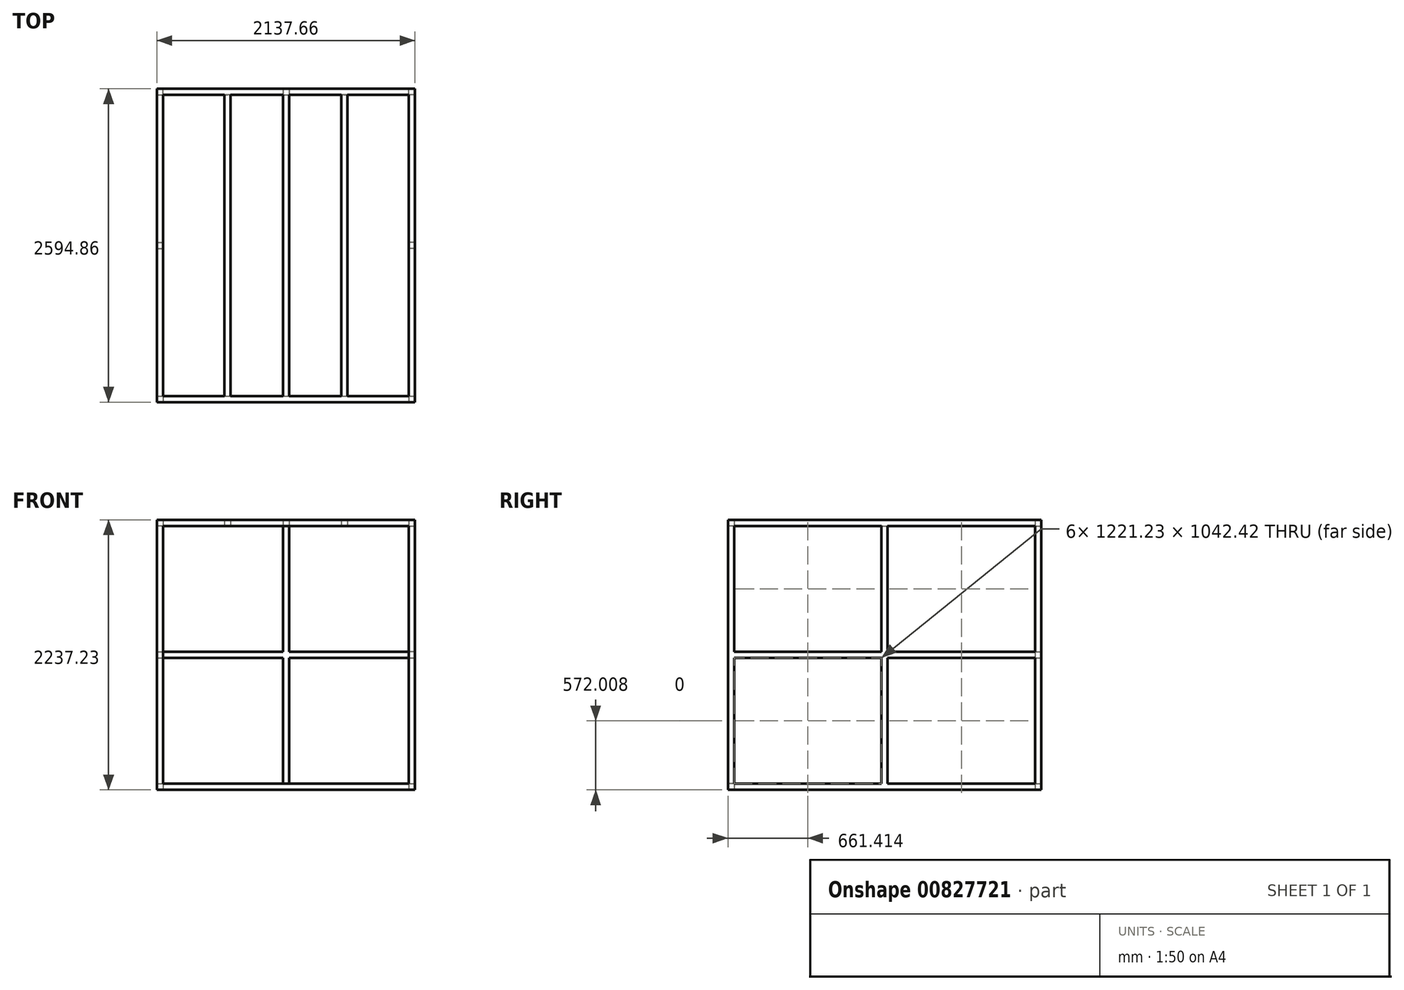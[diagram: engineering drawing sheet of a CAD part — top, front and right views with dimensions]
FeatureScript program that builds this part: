
annotation { "Feature Type Name" : "Feature", "Feature Type Description" : "" }
export const myFeature = defineFeature(function(context is Context, id is Id, definition is map)
    precondition{}
    {
        {
            var Q0;
            Q0=qCreatedBy(makeId("Top.planeOp"),FACE);
            var sketch = newSketch(context, id + "F0", { "sketchPlane" : qUnion([Q0])});
            skLineSegment(sketch, "E0.bottom", {"start": v(-1018.03, 1246.63) * mm, "end": v(1018.03, 1246.63) * mm});
            skLineSegment(sketch, "E0.top", {"start": v(-1018.03, -1246.63) * mm, "end": v(1018.03, -1246.63) * mm});
            skLineSegment(sketch, "E0.left", {"start": v(-1018.03, 1246.63) * mm, "end": v(-1018.03, -1246.63) * mm});
            skLineSegment(sketch, "E0.right", {"start": v(1018.03, 1246.63) * mm, "end": v(1018.03, -1246.63) * mm});
            skPoint(sketch, "E0.middle", {"position": v(0, 0) * mm});
            skLineSegment(sketch, "E1.bottom", {"start": v(-1068.83, 1297.43) * mm, "end": v(1068.83, 1297.43) * mm});
            skLineSegment(sketch, "E1.top", {"start": v(-1068.83, -1297.43) * mm, "end": v(1068.83, -1297.43) * mm});
            skLineSegment(sketch, "E1.left", {"start": v(-1068.83, 1297.43) * mm, "end": v(-1068.83, -1297.43) * mm});
            skLineSegment(sketch, "E1.right", {"start": v(1068.83, 1297.43) * mm, "end": v(1068.83, -1297.43) * mm});
            skLineSegment(sketch, "E2.bottom", {"start": v(-510.03, 1246.63) * mm, "end": v(-459.23, 1246.63) * mm});
            skLineSegment(sketch, "E2.top", {"start": v(-510.03, -1246.63) * mm, "end": v(-459.23, -1246.63) * mm});
            skLineSegment(sketch, "E2.left", {"start": v(-510.03, 1246.63) * mm, "end": v(-510.03, -1246.63) * mm});
            skLineSegment(sketch, "E2.right", {"start": v(-459.23, 1246.63) * mm, "end": v(-459.23, -1246.63) * mm});
            skLineSegment(sketch, "E3.bottom", {"start": v(459.23, -1246.63) * mm, "end": v(510.03, -1246.63) * mm});
            skLineSegment(sketch, "E3.top", {"start": v(459.23, 1246.63) * mm, "end": v(510.03, 1246.63) * mm});
            skLineSegment(sketch, "E3.left", {"start": v(459.23, -1246.63) * mm, "end": v(459.23, 1246.63) * mm});
            skLineSegment(sketch, "E3.right", {"start": v(510.03, -1246.63) * mm, "end": v(510.03, 1246.63) * mm});
            skLineSegment(sketch, "E4.bottom", {"start": v(-25.4, 1246.63) * mm, "end": v(25.4, 1246.63) * mm});
            skLineSegment(sketch, "E4.top", {"start": v(-25.4, -1246.63) * mm, "end": v(25.4, -1246.63) * mm});
            skLineSegment(sketch, "E4.left", {"start": v(-25.4, 1246.63) * mm, "end": v(-25.4, -1246.63) * mm});
            skLineSegment(sketch, "E4.right", {"start": v(25.4, 1246.63) * mm, "end": v(25.4, -1246.63) * mm});
            skSolve(sketch);
        }
        {
            var Q0;
            Q0=makeQuery(id+"F0.imprint","IMPRINT",FACE,{"disambiguationData":[TD([[makeQuery(id+"F0.imprint","IMPRINT",EDGE,{"derivedFrom":sQuery(id+"F0.wireOp",EDGE,"E0.bottom")}),1.0]])]});
            var Q1;
            Q1=makeQuery(id+"F0.imprint","IMPRINT",FACE,{"disambiguationData":[TD([[makeQuery(id+"F0.imprint","IMPRINT",EDGE,{"derivedFrom":sQuery(id+"F0.wireOp",EDGE,"E2.bottom")}),-1.0]])]});
            var Q2;
            Q2=makeQuery(id+"F0.imprint","IMPRINT",FACE,{"disambiguationData":[TD([[makeQuery(id+"F0.imprint","IMPRINT",EDGE,{"derivedFrom":sQuery(id+"F0.wireOp",EDGE,"E4.bottom")}),-1.0]])]});
            var Q3;
            Q3=makeQuery(id+"F0.imprint","IMPRINT",FACE,{"disambiguationData":[TD([[makeQuery(id+"F0.imprint","IMPRINT",EDGE,{"derivedFrom":sQuery(id+"F0.wireOp",EDGE,"E3.bottom")}),1.0]])]});
            extrude(context, id + "F1", {"entities" : qUnion([Q0, Q1, Q2, Q3]), "depth" : 50.8 * mm, "offsetDistance" : 25.4 * mm});
        }
        {
            var Q0;
            Q0=makeQuery(id+"F1.opExtrude","CAP_FACE",FACE,{"disambiguationData":[OSD([sQuery(id+"F0.wireOp",EDGE,"E0.bottom"),sQuery(id+"F0.wireOp",EDGE,"E0.top"),sQuery(id+"F0.wireOp",EDGE,"E0.left"),sQuery(id+"F0.wireOp",EDGE,"E0.right"),sQuery(id+"F0.wireOp",EDGE,"E1.bottom"),sQuery(id+"F0.wireOp",EDGE,"E1.top"),sQuery(id+"F0.wireOp",EDGE,"E1.left"),sQuery(id+"F0.wireOp",EDGE,"E1.right")])],"isStart":false});
            var sketch = newSketch(context, id + "F2", { "sketchPlane" : qUnion([Q0])});
            skLineSegment(sketch, "E5.bottom", {"start": v(-1018.03, 1246.63) * mm, "end": v(-1068.83, 1246.63) * mm});
            skLineSegment(sketch, "E5.top", {"start": v(-1018.03, 1297.43) * mm, "end": v(-1068.83, 1297.43) * mm});
            skLineSegment(sketch, "E5.left", {"start": v(-1018.03, 1246.63) * mm, "end": v(-1018.03, 1297.43) * mm});
            skLineSegment(sketch, "E5.right", {"start": v(-1068.83, 1246.63) * mm, "end": v(-1068.83, 1297.43) * mm});
            skLineSegment(sketch, "E6.bottom", {"start": v(1018.03, 1246.63) * mm, "end": v(1068.83, 1246.63) * mm});
            skLineSegment(sketch, "E6.top", {"start": v(1018.03, 1297.43) * mm, "end": v(1068.83, 1297.43) * mm});
            skLineSegment(sketch, "E6.left", {"start": v(1018.03, 1246.63) * mm, "end": v(1018.03, 1297.43) * mm});
            skLineSegment(sketch, "E6.right", {"start": v(1068.83, 1246.63) * mm, "end": v(1068.83, 1297.43) * mm});
            skLineSegment(sketch, "E7.bottom", {"start": v(1018.03, -1246.63) * mm, "end": v(1068.83, -1246.63) * mm});
            skLineSegment(sketch, "E7.top", {"start": v(1018.03, -1297.43) * mm, "end": v(1068.83, -1297.43) * mm});
            skLineSegment(sketch, "E7.left", {"start": v(1018.03, -1246.63) * mm, "end": v(1018.03, -1297.43) * mm});
            skLineSegment(sketch, "E7.right", {"start": v(1068.83, -1246.63) * mm, "end": v(1068.83, -1297.43) * mm});
            skLineSegment(sketch, "E8.bottom", {"start": v(-1018.03, -1246.63) * mm, "end": v(-1068.83, -1246.63) * mm});
            skLineSegment(sketch, "E8.top", {"start": v(-1018.03, -1297.43) * mm, "end": v(-1068.83, -1297.43) * mm});
            skLineSegment(sketch, "E8.left", {"start": v(-1018.03, -1246.63) * mm, "end": v(-1018.03, -1297.43) * mm});
            skLineSegment(sketch, "E8.right", {"start": v(-1068.83, -1246.63) * mm, "end": v(-1068.83, -1297.43) * mm});
            skLineSegment(sketch, "E9.bottom", {"start": v(-1068.83, 25.4) * mm, "end": v(-1018.03, 25.4) * mm});
            skLineSegment(sketch, "E9.top", {"start": v(-1068.83, -25.4) * mm, "end": v(-1018.03, -25.4) * mm});
            skLineSegment(sketch, "E9.left", {"start": v(-1068.83, 25.4) * mm, "end": v(-1068.83, -25.4) * mm});
            skLineSegment(sketch, "E9.right", {"start": v(-1018.03, 25.4) * mm, "end": v(-1018.03, -25.4) * mm});
            skLineSegment(sketch, "E10.bottom", {"start": v(1018.03, -25.4) * mm, "end": v(1068.83, -25.4) * mm});
            skLineSegment(sketch, "E10.top", {"start": v(1018.03, 25.4) * mm, "end": v(1068.83, 25.4) * mm});
            skLineSegment(sketch, "E10.left", {"start": v(1018.03, -25.4) * mm, "end": v(1018.03, 25.4) * mm});
            skLineSegment(sketch, "E10.right", {"start": v(1068.83, -25.4) * mm, "end": v(1068.83, 25.4) * mm});
            skLineSegment(sketch, "E11.bottom", {"start": v(-25.4, 1297.43) * mm, "end": v(25.4, 1297.43) * mm});
            skLineSegment(sketch, "E11.top", {"start": v(-25.4, 1246.63) * mm, "end": v(25.4, 1246.63) * mm});
            skLineSegment(sketch, "E11.left", {"start": v(-25.4, 1297.43) * mm, "end": v(-25.4, 1246.63) * mm});
            skLineSegment(sketch, "E11.right", {"start": v(25.4, 1297.43) * mm, "end": v(25.4, 1246.63) * mm});
            skSolve(sketch);
        }
        {
            var Q0;
            Q0=makeQuery(id+"F2.imprint","IMPRINT",FACE,{"disambiguationData":[TD([[makeQuery(id+"F2.imprint","IMPRINT",EDGE,{"derivedFrom":sQuery(id+"F2.wireOp",EDGE,"E5.bottom")}),-1.0]])]});
            var Q1;
            Q1=makeQuery(id+"F2.imprint","IMPRINT",FACE,{"disambiguationData":[TD([[makeQuery(id+"F2.imprint","IMPRINT",EDGE,{"derivedFrom":sQuery(id+"F2.wireOp",EDGE,"E6.bottom")}),1.0]])]});
            var Q2;
            Q2=makeQuery(id+"F2.imprint","IMPRINT",FACE,{"disambiguationData":[TD([[makeQuery(id+"F2.imprint","IMPRINT",EDGE,{"derivedFrom":sQuery(id+"F2.wireOp",EDGE,"E7.bottom")}),-1.0]])]});
            var Q3;
            Q3=makeQuery(id+"F2.imprint","IMPRINT",FACE,{"disambiguationData":[TD([[makeQuery(id+"F2.imprint","IMPRINT",EDGE,{"derivedFrom":sQuery(id+"F2.wireOp",EDGE,"E8.bottom")}),1.0]])]});
            var Q4;
            Q4=makeQuery(id+"F2.imprint","IMPRINT",FACE,{"disambiguationData":[TD([[makeQuery(id+"F2.imprint","IMPRINT",EDGE,{"derivedFrom":sQuery(id+"F2.wireOp",EDGE,"E9.bottom")}),-1.0]])]});
            var Q5;
            Q5=makeQuery(id+"F2.imprint","IMPRINT",FACE,{"disambiguationData":[TD([[makeQuery(id+"F2.imprint","IMPRINT",EDGE,{"derivedFrom":sQuery(id+"F2.wireOp",EDGE,"E10.bottom")}),1.0]])]});
            var Q6;
            Q6=makeQuery(id+"F2.imprint","IMPRINT",FACE,{"disambiguationData":[TD([[makeQuery(id+"F2.imprint","IMPRINT",EDGE,{"derivedFrom":sQuery(id+"F2.wireOp",EDGE,"E11.bottom")}),-1.0]])]});
            extrude(context, id + "F3", {"entities" : qUnion([Q0, Q1, Q2, Q3, Q4, Q5, Q6]), "operationType" : NewBodyOperationType.ADD, "depth" : 2135.63 * mm, "offsetDistance" : 25.4 * mm});
        }
        {
            var Q0;
            Q0=makeQuery(id+"F3.opExtrude","CAP_FACE",FACE,{"disambiguationData":[OSD([sQuery(id+"F2.wireOp",EDGE,"E5.bottom"),sQuery(id+"F2.wireOp",EDGE,"E5.top"),sQuery(id+"F2.wireOp",EDGE,"E5.left"),sQuery(id+"F2.wireOp",EDGE,"E5.right")])],"isStart":false});
            var sketch = newSketch(context, id + "F4", { "sketchPlane" : qUnion([Q0])});
            skLineSegment(sketch, "E12.0", {"start": v(-1068.83, 1246.63) * mm, "end": v(-1068.83, 25.4) * mm});
            skLineSegment(sketch, "E13.0", {"start": v(-1018.03, 1246.63) * mm, "end": v(-1018.03, 25.4) * mm});
            skLineSegment(sketch, "E14.0", {"start": v(-1018.03, 1246.63) * mm, "end": v(-510.03, 1246.63) * mm});
            skLineSegment(sketch, "E15.0", {"start": v(-1018.03, 1297.43) * mm, "end": v(-25.4, 1297.43) * mm});
            skLineSegment(sketch, "E16.0", {"start": v(-510.03, 1246.63) * mm, "end": v(-510.03, -1246.63) * mm});
            skLineSegment(sketch, "E17.0", {"start": v(-459.23, 1246.63) * mm, "end": v(-25.4, 1246.63) * mm});
            skLineSegment(sketch, "E18.0", {"start": v(-25.4, 1246.63) * mm, "end": v(-25.4, -1246.63) * mm});
            skLineSegment(sketch, "E19.0", {"start": v(25.4, 1246.63) * mm, "end": v(25.4, -1246.63) * mm});
            skLineSegment(sketch, "E20.0.0", {"start": v(1018.03, 1297.43) * mm, "end": v(25.4, 1297.43) * mm});
            skLineSegment(sketch, "E20.0.2", {"start": v(25.4, 1246.63) * mm, "end": v(459.23, 1246.63) * mm});
            skLineSegment(sketch, "E20.0.3", {"start": v(459.23, 1246.63) * mm, "end": v(459.23, -1246.63) * mm});
            skLineSegment(sketch, "E20.0.4", {"start": v(459.23, -1246.63) * mm, "end": v(25.4, -1246.63) * mm});
            skLineSegment(sketch, "E20.0.5", {"start": v(25.4, -1246.63) * mm, "end": v(25.4, 1246.63) * mm});
            skLineSegment(sketch, "E20.0.8", {"start": v(-25.4, -1246.63) * mm, "end": v(-459.23, -1246.63) * mm});
            skLineSegment(sketch, "E20.0.9", {"start": v(-459.23, -1246.63) * mm, "end": v(-459.23, 1246.63) * mm});
            skLineSegment(sketch, "E20.0.12", {"start": v(-25.4, 1297.43) * mm, "end": v(-1018.03, 1297.43) * mm});
            skLineSegment(sketch, "E20.0.16", {"start": v(-510.03, -1246.63) * mm, "end": v(-1018.03, -1246.63) * mm});
            skLineSegment(sketch, "E20.0.18", {"start": v(-1018.03, -1297.43) * mm, "end": v(1018.03, -1297.43) * mm});
            skLineSegment(sketch, "E20.0.20", {"start": v(1018.03, -1246.63) * mm, "end": v(510.03, -1246.63) * mm});
            skLineSegment(sketch, "E20.0.21", {"start": v(510.03, -1246.63) * mm, "end": v(510.03, 1246.63) * mm});
            skLineSegment(sketch, "E20.0.22", {"start": v(510.03, 1246.63) * mm, "end": v(1018.03, 1246.63) * mm});
            skPoint(sketch, "E21.0", {"position": v(0, 1297.43) * mm});
            skLineSegment(sketch, "E22.0", {"start": v(1068.83, -25.4) * mm, "end": v(1068.83, -1246.63) * mm});
            skLineSegment(sketch, "E23.0.1", {"start": v(1018.03, -25.4) * mm, "end": v(1018.03, -1246.63) * mm});
            skLineSegment(sketch, "E23.0.3", {"start": v(1068.83, -1246.63) * mm, "end": v(1068.83, -25.4) * mm});
            skLineSegment(sketch, "E24.0", {"start": v(1018.03, 25.4) * mm, "end": v(1018.03, -25.4) * mm});
            skLineSegment(sketch, "E25.0", {"start": v(1068.83, 25.4) * mm, "end": v(1068.83, -25.4) * mm});
            skLineSegment(sketch, "E26.0", {"start": v(1018.03, 1246.63) * mm, "end": v(1018.03, 25.4) * mm});
            skLineSegment(sketch, "E27.0", {"start": v(1068.83, 1246.63) * mm, "end": v(1068.83, 25.4) * mm});
            skLineSegment(sketch, "E28.0", {"start": v(1018.03, 1297.43) * mm, "end": v(1068.83, 1297.43) * mm});
            skLineSegment(sketch, "E29.0", {"start": v(1068.83, 1297.43) * mm, "end": v(1068.83, 1246.63) * mm});
            skLineSegment(sketch, "E30.0", {"start": v(-1068.83, -1246.63) * mm, "end": v(-1068.83, -1297.43) * mm});
            skLineSegment(sketch, "E31.0", {"start": v(-1068.83, -1297.43) * mm, "end": v(-1018.03, -1297.43) * mm});
            skLineSegment(sketch, "E32.0", {"start": v(-1018.03, -25.4) * mm, "end": v(-1018.03, -1246.63) * mm});
            skLineSegment(sketch, "E33.0", {"start": v(-1068.83, -25.4) * mm, "end": v(-1068.83, -1246.63) * mm});
            skLineSegment(sketch, "E34.0", {"start": v(-1068.83, 25.4) * mm, "end": v(-1068.83, -25.4) * mm});
            skLineSegment(sketch, "E35.0", {"start": v(-1018.03, 25.4) * mm, "end": v(-1018.03, -25.4) * mm});
            skLineSegment(sketch, "E36", {"start": v(25.4, 1297.43) * mm, "end": v(-25.4, 1297.43) * mm});
            skLineSegment(sketch, "E37", {"start": v(1018.03, -1297.43) * mm, "end": v(1068.83, -1297.43) * mm});
            skLineSegment(sketch, "E38", {"start": v(1068.83, -1297.43) * mm, "end": v(1068.83, -1246.63) * mm});
            skLineSegment(sketch, "E39", {"start": v(-1068.83, 1246.63) * mm, "end": v(-1068.83, 1297.43) * mm});
            skLineSegment(sketch, "E40", {"start": v(-1068.83, 1297.43) * mm, "end": v(-1018.03, 1297.43) * mm});
            skSolve(sketch);
        }
        {
            var Q0;
            Q0 = qSketchRegion(id + "F4", true);
            extrude(context, id + "F5", {"entities" : qUnion([Q0]), "operationType" : NewBodyOperationType.ADD, "depth" : 50.8 * mm, "offsetDistance" : 25.4 * mm});
        }
        {
            var Q0;
            Q0=makeQuery(id+"F3.opExtrude","SWEPT_FACE",FACE,{"disambiguationData":[OSD([sQuery(id+"F2.wireOp",EDGE,"E5.bottom")])]});
            var sketch = newSketch(context, id + "F6", { "sketchPlane" : qUnion([Q0])});
            skLineSegment(sketch, "E41.bottom", {"start": v(-1068.83, 1093.22) * mm, "end": v(-1018.03, 1093.22) * mm});
            skLineSegment(sketch, "E41.top", {"start": v(-1068.83, 1144.02) * mm, "end": v(-1018.03, 1144.02) * mm});
            skLineSegment(sketch, "E41.left", {"start": v(-1068.83, 1093.22) * mm, "end": v(-1068.83, 1144.02) * mm});
            skLineSegment(sketch, "E41.right", {"start": v(-1018.03, 1093.22) * mm, "end": v(-1018.03, 1144.02) * mm});
            skSolve(sketch);
        }
        {
            var Q0;
            Q0=makeQuery(id+"F6.imprint","IMPRINT",FACE,{"disambiguationData":[TD([[makeQuery(id+"F6.imprint","IMPRINT",EDGE,{"derivedFrom":sQuery(id+"F6.wireOp",EDGE,"E41.bottom")}),1.0]])]});
            var Q1;
            Q1=makeQuery(id+"F3.opExtrude","SWEPT_FACE",FACE,{"disambiguationData":[OSD([sQuery(id+"F2.wireOp",EDGE,"E8.bottom")])]});
            extrude(context, id + "F7", {"entities" : qUnion([Q0]), "operationType" : NewBodyOperationType.ADD, "endBound" : BoundingType.UP_TO_SURFACE, "depth" : 25.4 * mm, "endBoundEntityFace" : qUnion([Q1]), "offsetDistance" : 25.4 * mm});
        }
        {
            var Q0;
            Q0=makeQuery(id+"F3.opExtrude","SWEPT_FACE",FACE,{"disambiguationData":[OSD([sQuery(id+"F2.wireOp",EDGE,"E6.bottom")])]});
            var sketch = newSketch(context, id + "F8", { "sketchPlane" : qUnion([Q0])});
            skLineSegment(sketch, "E42.bottom", {"start": v(1068.83, 1093.22) * mm, "end": v(1018.03, 1093.22) * mm});
            skLineSegment(sketch, "E42.top", {"start": v(1068.83, 1144.02) * mm, "end": v(1018.03, 1144.02) * mm});
            skLineSegment(sketch, "E42.left", {"start": v(1068.83, 1093.22) * mm, "end": v(1068.83, 1144.02) * mm});
            skLineSegment(sketch, "E42.right", {"start": v(1018.03, 1093.22) * mm, "end": v(1018.03, 1144.02) * mm});
            skSolve(sketch);
        }
        {
            var Q0;
            Q0=makeQuery(id+"F8.imprint","IMPRINT",FACE,{"disambiguationData":[TD([[makeQuery(id+"F8.imprint","IMPRINT",EDGE,{"derivedFrom":sQuery(id+"F8.wireOp",EDGE,"E42.bottom")}),-1.0]])]});
            var Q1;
            Q1=makeQuery(id+"F3.opExtrude","SWEPT_FACE",FACE,{"disambiguationData":[OSD([sQuery(id+"F2.wireOp",EDGE,"E7.bottom")])]});
            extrude(context, id + "F9", {"entities" : qUnion([Q0]), "operationType" : NewBodyOperationType.ADD, "endBound" : BoundingType.UP_TO_SURFACE, "depth" : 25.4 * mm, "endBoundEntityFace" : qUnion([Q1]), "offsetDistance" : 25.4 * mm});
        }
        {
            var Q0;
            Q0=makeQuery(id+"F7.boolean.opBoolean","MERGE",FACE,{"derivedFrom":[makeQuery(id+"F3.opExtrude","SWEPT_FACE",FACE,{"disambiguationData":[OSD([sQuery(id+"F2.wireOp",EDGE,"E5.left")])]}),makeQuery(id+"F3.opExtrude","SWEPT_FACE",FACE,{"disambiguationData":[OSD([sQuery(id+"F2.wireOp",EDGE,"E8.left")])]}),makeQuery(id+"F5.boolean.opBoolean","MERGE",FACE,{"derivedFrom":[makeQuery(id+"F3.boolean.opBoolean","MERGE",FACE,{"derivedFrom":[makeQuery(id+"F1.opExtrude","SWEPT_FACE",FACE,{"disambiguationData":[OSD([sQuery(id+"F0.wireOp",EDGE,"E0.left")])]}),makeQuery(id+"F3.opExtrude","SWEPT_FACE",FACE,{"disambiguationData":[OSD([sQuery(id+"F2.wireOp",EDGE,"E9.right")])]})]}),makeQuery(id+"F5.opExtrude","SWEPT_FACE",FACE,{"disambiguationData":[OSD([sQuery(id+"F4.wireOp",EDGE,"E13.0"),sQuery(id+"F4.wireOp",EDGE,"E32.0"),sQuery(id+"F4.wireOp",EDGE,"E35.0")])]})]}),makeQuery(id+"F7.opExtrude","SWEPT_FACE",FACE,{"disambiguationData":[OSD([sQuery(id+"F6.wireOp",EDGE,"E41.right")])]})]});
            var sketch = newSketch(context, id + "F10", { "sketchPlane" : qUnion([Q0])});
            skLineSegment(sketch, "E43.bottom", {"start": v(1246.63, 1144.02) * mm, "end": v(1297.43, 1144.02) * mm});
            skLineSegment(sketch, "E43.top", {"start": v(1246.63, 1093.22) * mm, "end": v(1297.43, 1093.22) * mm});
            skLineSegment(sketch, "E43.left", {"start": v(1246.63, 1144.02) * mm, "end": v(1246.63, 1093.22) * mm});
            skLineSegment(sketch, "E43.right", {"start": v(1297.43, 1144.02) * mm, "end": v(1297.43, 1093.22) * mm});
            skSolve(sketch);
        }
        {
            var Q0;
            Q0=makeQuery(id+"F10.imprint","IMPRINT",FACE,{"disambiguationData":[TD([[makeQuery(id+"F10.imprint","IMPRINT",EDGE,{"derivedFrom":sQuery(id+"F10.wireOp",EDGE,"E43.bottom")}),-1.0]])]});
            var Q1;
            Q1=makeQuery(id+"F9.boolean.opBoolean","MERGE",FACE,{"derivedFrom":[makeQuery(id+"F3.opExtrude","SWEPT_FACE",FACE,{"disambiguationData":[OSD([sQuery(id+"F2.wireOp",EDGE,"E6.left")])]}),makeQuery(id+"F3.opExtrude","SWEPT_FACE",FACE,{"disambiguationData":[OSD([sQuery(id+"F2.wireOp",EDGE,"E7.left")])]}),makeQuery(id+"F5.boolean.opBoolean","MERGE",FACE,{"derivedFrom":[makeQuery(id+"F3.boolean.opBoolean","MERGE",FACE,{"derivedFrom":[makeQuery(id+"F1.opExtrude","SWEPT_FACE",FACE,{"disambiguationData":[OSD([sQuery(id+"F0.wireOp",EDGE,"E0.right")])]}),makeQuery(id+"F3.opExtrude","SWEPT_FACE",FACE,{"disambiguationData":[OSD([sQuery(id+"F2.wireOp",EDGE,"E10.left")])]})]}),makeQuery(id+"F5.opExtrude","SWEPT_FACE",FACE,{"disambiguationData":[OSD([sQuery(id+"F4.wireOp",EDGE,"E23.0.1"),sQuery(id+"F4.wireOp",EDGE,"E24.0"),sQuery(id+"F4.wireOp",EDGE,"E26.0")])]})]}),makeQuery(id+"F9.opExtrude","SWEPT_FACE",FACE,{"disambiguationData":[OSD([sQuery(id+"F8.wireOp",EDGE,"E42.right")])]})]});
            extrude(context, id + "F11", {"entities" : qUnion([Q0]), "operationType" : NewBodyOperationType.ADD, "endBound" : BoundingType.UP_TO_SURFACE, "depth" : 25.4 * mm, "endBoundEntityFace" : qUnion([Q1]), "offsetDistance" : 25.4 * mm});
        }
    });
